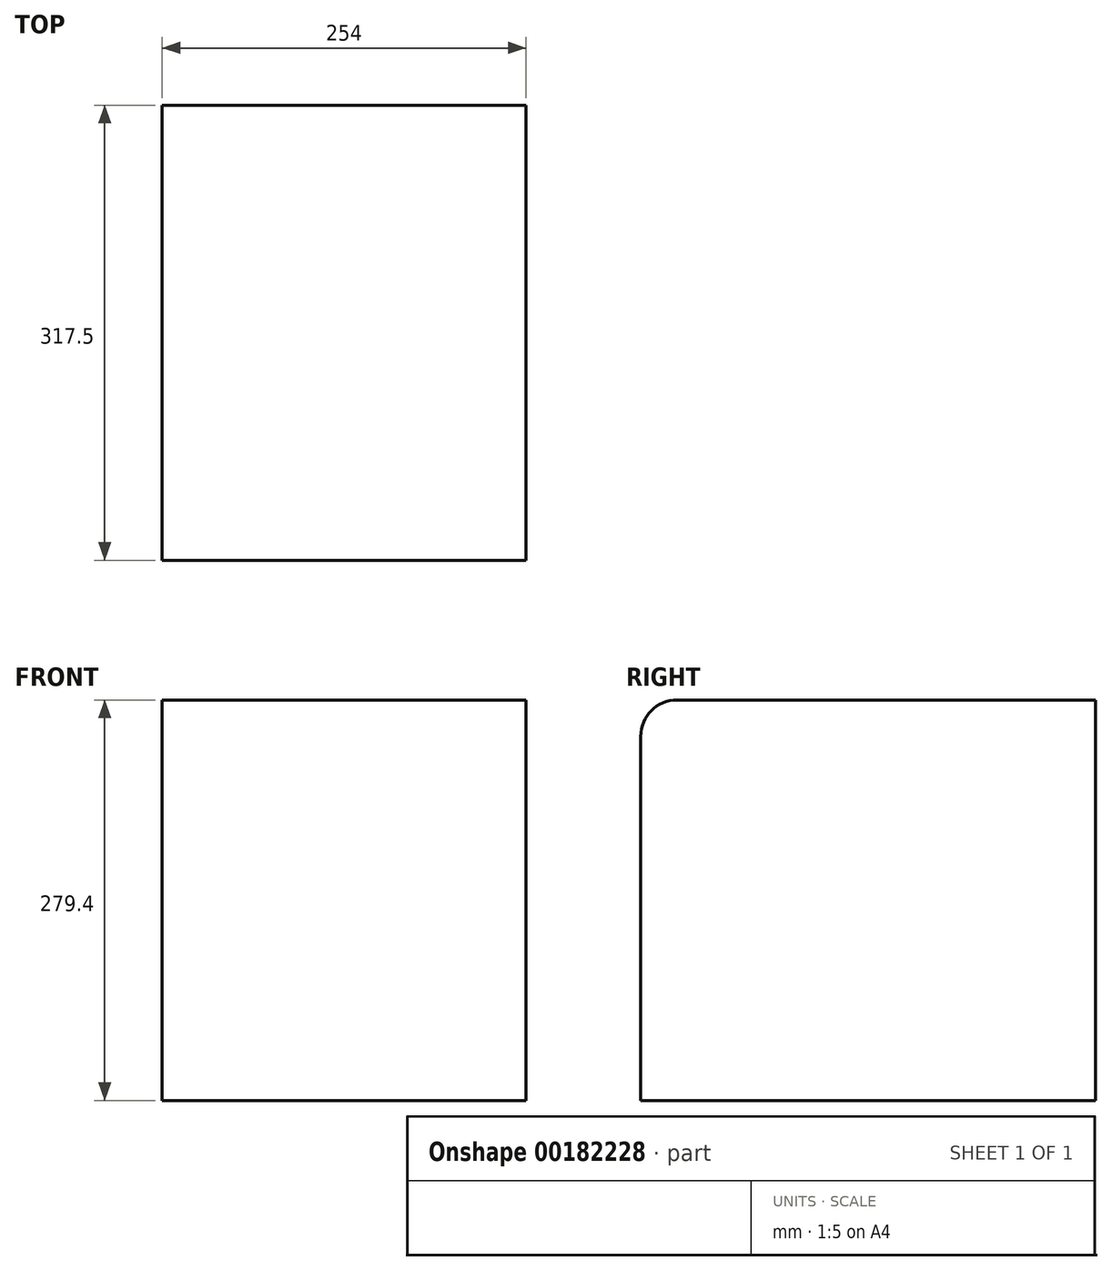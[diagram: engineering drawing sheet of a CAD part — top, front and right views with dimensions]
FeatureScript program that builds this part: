
annotation { "Feature Type Name" : "Feature", "Feature Type Description" : "" }
export const myFeature = defineFeature(function(context is Context, id is Id, definition is map)
    precondition{}
    {
        {
            var Q0;
            Q0=qCreatedBy(makeId("Front.planeOp"),FACE);
            var sketch = newSketch(context, id + "F0", { "sketchPlane" : qUnion([Q0])});
            skLineSegment(sketch, "E0.bottom", {"start": v(0, 0) * mm, "end": v(254, 0) * mm});
            skLineSegment(sketch, "E0.top", {"start": v(0, 279.4) * mm, "end": v(254, 279.4) * mm});
            skLineSegment(sketch, "E0.left", {"start": v(0, 0) * mm, "end": v(0, 279.4) * mm});
            skLineSegment(sketch, "E0.right", {"start": v(254, 0) * mm, "end": v(254, 279.4) * mm});
            skSolve(sketch);
        }
        {
            var Q0;
            Q0=qSketchRegion(id+"F0",true);
            extrude(context, id + "F1", {"entities" : qUnion([Q0]), "oppositeDirection" : true, "depth" : 317.5 * mm});
        }
        {
            var Q0;
            Q0=makeQuery(id+"F1.opExtrude","CAP_EDGE",EDGE,{"disambiguationData":[OSD([sQuery(id+"F0.wireOp",EDGE,"E0.top")])],"isStart":true});
            fillet(context, id + "F2", {"entities" : qUnion([Q0]), "radius" : 25.4 * mm, "tangentPropagation" : true, "allowEdgeOverflow" : false});
        }
    });
